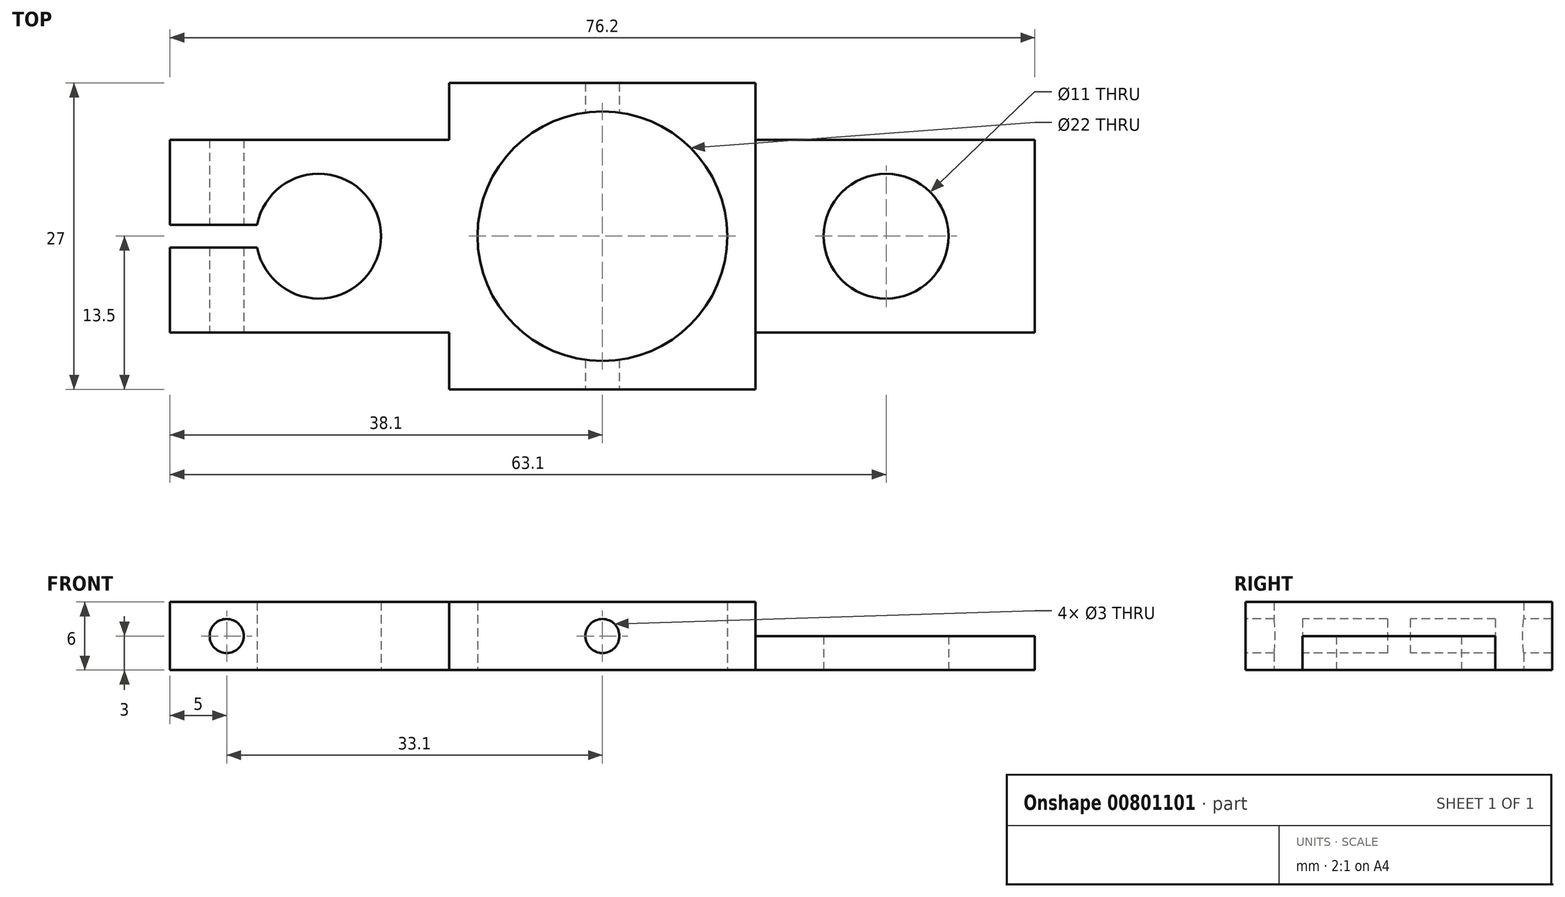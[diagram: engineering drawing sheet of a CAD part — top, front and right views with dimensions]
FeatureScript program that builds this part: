
annotation { "Feature Type Name" : "Feature", "Feature Type Description" : "" }
export const myFeature = defineFeature(function(context is Context, id is Id, definition is map)
    precondition{}
    {
        {
            var Q0;
            Q0=qCreatedBy(makeId("Top.planeOp"),FACE);
            var sketch = newSketch(context, id + "F0", { "sketchPlane" : qUnion([Q0])});
            skCircle(sketch, "E0", {"center": v(0, 0) * mm, "radius": 11 * mm});
            skArc(sketch, "E1", {"start": v(-30.4, -1) * mm, "mid": v(-19.5, 0) * mm, "end": v(-30.4, 1) * mm});
            skCircle(sketch, "E2", {"center": v(25, 0) * mm, "radius": 5.5 * mm});
            skLineSegment(sketch, "E3.bottom", {"start": v(-38.1, 8.5) * mm, "end": v(-13.5, 8.5) * mm});
            skLineSegment(sketch, "E3.top", {"start": v(-38.1, -8.5) * mm, "end": v(-13.5, -8.5) * mm});
            skLineSegment(sketch, "E3.left", {"start": v(-38.1, 8.5) * mm, "end": v(-38.1, 1) * mm});
            skLineSegment(sketch, "E3.right", {"start": v(38.1, 8.5) * mm, "end": v(38.1, -8.5) * mm});
            skLineSegment(sketch, "E4.bottom", {"start": v(13.5, -13.5) * mm, "end": v(-13.5, -13.5) * mm});
            skLineSegment(sketch, "E4.top", {"start": v(13.5, 13.5) * mm, "end": v(-13.5, 13.5) * mm});
            skLineSegment(sketch, "E4.left", {"start": v(13.5, -13.5) * mm, "end": v(13.5, -8.5) * mm});
            skLineSegment(sketch, "E4.right", {"start": v(-13.5, -13.5) * mm, "end": v(-13.5, -8.5) * mm});
            skLineSegment(sketch, "E5.trimOffspring", {"start": v(13.5, 8.5) * mm, "end": v(38.1, 8.5) * mm});
            skLineSegment(sketch, "E6.trimOffspring", {"start": v(13.5, -8.5) * mm, "end": v(38.1, -8.5) * mm});
            skLineSegment(sketch, "E7.trimOffspring", {"start": v(-13.5, 8.5) * mm, "end": v(-13.5, 13.5) * mm});
            skLineSegment(sketch, "E8.trimOffspring", {"start": v(13.5, 8.5) * mm, "end": v(13.5, 13.5) * mm});
            skLineSegment(sketch, "E9", {"start": v(-38.1, 1) * mm, "end": v(-30.4, 1) * mm});
            skLineSegment(sketch, "E10", {"start": v(-38.1, -1) * mm, "end": v(-30.4, -1) * mm});
            skLineSegment(sketch, "E11.trimOffspring", {"start": v(-38.1, -1) * mm, "end": v(-38.1, -8.5) * mm});
            skSolve(sketch);
        }
        {
            var Q0;
            Q0 = qSketchRegion(id + "F0", true);
            extrude(context, id + "F1", {"entities" : qUnion([Q0]), "depth" : 6 * mm, "offsetDistance" : 25.4 * mm});
        }
        {
            var Q0;
            Q0=makeQuery(id+"F1.opExtrude","SWEPT_FACE",FACE,{"disambiguationData":[OSD([sQuery(id+"F0.wireOp",EDGE,"E4.bottom")])]});
            var sketch = newSketch(context, id + "F2", { "sketchPlane" : qUnion([Q0])});
            skCircle(sketch, "E12", {"center": v(0, 3) * mm, "radius": 1.5 * mm});
            skCircle(sketch, "E13", {"center": v(-33.1, 3) * mm, "radius": 1.5 * mm});
            skSolve(sketch);
        }
        {
            var Q0;
            Q0 = qSketchRegion(id + "F2", true);
            extrude(context, id + "F3", {"entities" : qUnion([Q0]), "operationType" : NewBodyOperationType.REMOVE, "oppositeDirection" : true, "depth" : 50.8 * mm, "offsetDistance" : 25.4 * mm});
        }
        {
            var Q0;
            Q0=makeQuery(id+"F1.opExtrude","CAP_FACE",FACE,{"disambiguationData":[OSD([sQuery(id+"F0.wireOp",EDGE,"E0"),sQuery(id+"F0.wireOp",EDGE,"E1"),sQuery(id+"F0.wireOp",EDGE,"E2"),sQuery(id+"F0.wireOp",EDGE,"E3.bottom"),sQuery(id+"F0.wireOp",EDGE,"E3.top"),sQuery(id+"F0.wireOp",EDGE,"E3.left"),sQuery(id+"F0.wireOp",EDGE,"E3.right"),sQuery(id+"F0.wireOp",EDGE,"E4.bottom"),sQuery(id+"F0.wireOp",EDGE,"E4.top"),sQuery(id+"F0.wireOp",EDGE,"E4.left"),sQuery(id+"F0.wireOp",EDGE,"E4.right"),sQuery(id+"F0.wireOp",EDGE,"E5.trimOffspring"),sQuery(id+"F0.wireOp",EDGE,"E6.trimOffspring"),sQuery(id+"F0.wireOp",EDGE,"E7.trimOffspring"),sQuery(id+"F0.wireOp",EDGE,"E8.trimOffspring"),sQuery(id+"F0.wireOp",EDGE,"E9"),sQuery(id+"F0.wireOp",EDGE,"E10"),sQuery(id+"F0.wireOp",EDGE,"E11.trimOffspring")])],"isStart":false});
            var sketch = newSketch(context, id + "F4", { "sketchPlane" : qUnion([Q0])});
            skLineSegment(sketch, "E14.bottom", {"start": v(13.5, 13.5) * mm, "end": v(67.75, 13.5) * mm});
            skLineSegment(sketch, "E14.top", {"start": v(13.5, -19.1) * mm, "end": v(67.75, -19.1) * mm});
            skLineSegment(sketch, "E14.left", {"start": v(13.5, 13.5) * mm, "end": v(13.5, -19.1) * mm});
            skLineSegment(sketch, "E14.right", {"start": v(67.75, 13.5) * mm, "end": v(67.75, -19.1) * mm});
            skSolve(sketch);
        }
        {
            var Q0;
            Q0 = qSketchRegion(id + "F4", true);
            extrude(context, id + "F5", {"entities" : qUnion([Q0]), "operationType" : NewBodyOperationType.REMOVE, "oppositeDirection" : true, "depth" : 3 * mm, "offsetDistance" : 25.4 * mm});
        }
    });
